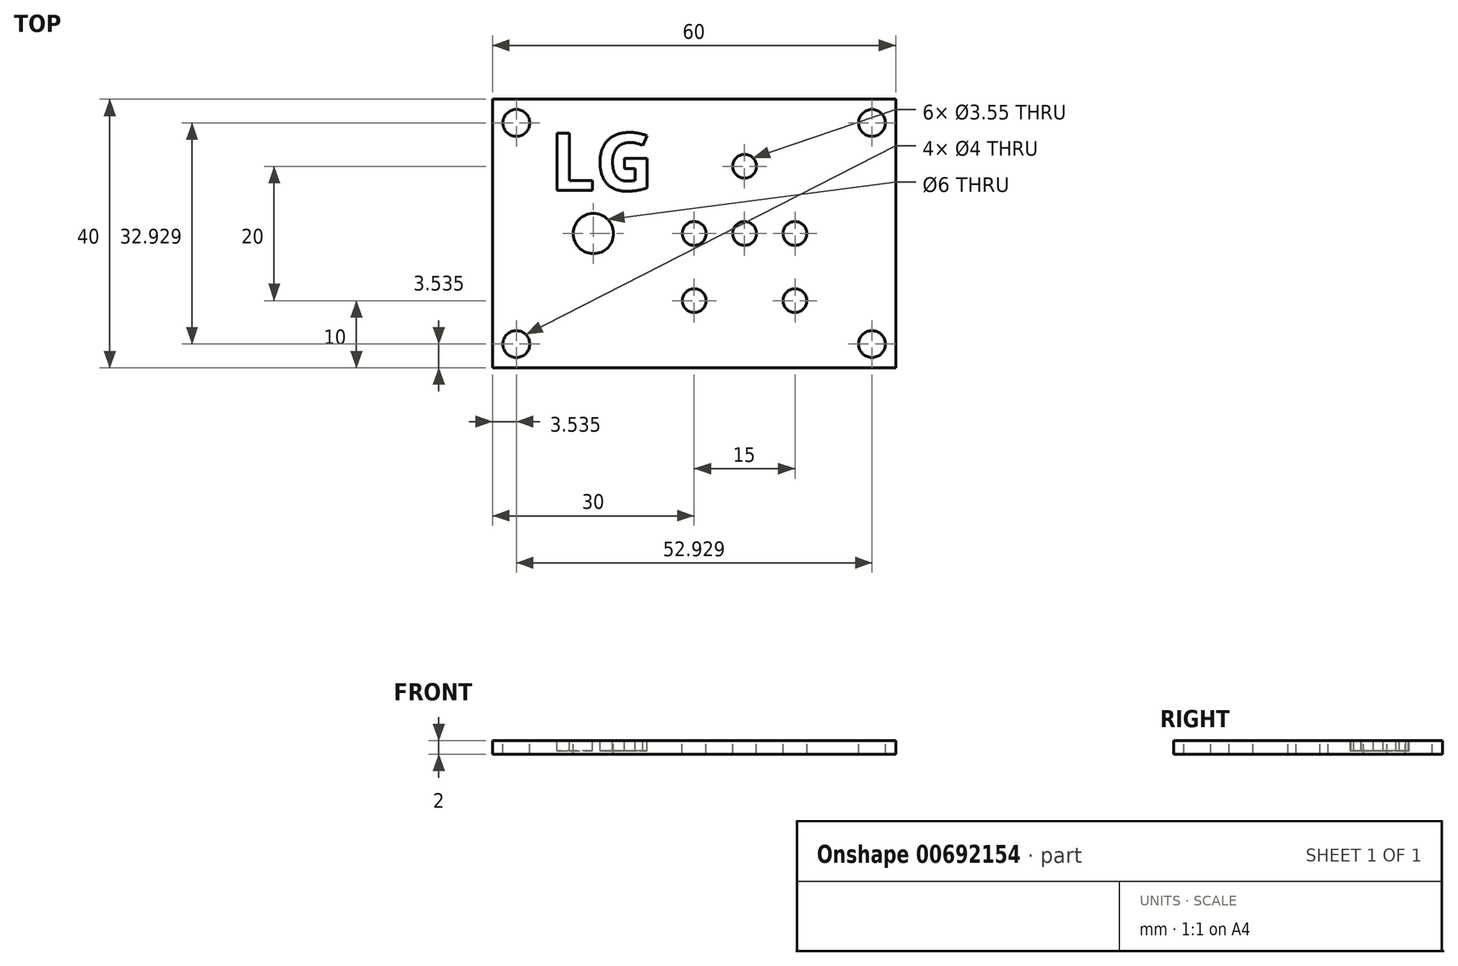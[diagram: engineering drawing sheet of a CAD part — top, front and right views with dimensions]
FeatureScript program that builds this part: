
annotation { "Feature Type Name" : "Feature", "Feature Type Description" : "" }
export const myFeature = defineFeature(function(context is Context, id is Id, definition is map)
    precondition{}
    {
        {
            var Q0;
            Q0=qCreatedBy(makeId("Top.planeOp"),FACE);
            var sketch = newSketch(context, id + "F0", { "sketchPlane" : qUnion([Q0])});
            skLineSegment(sketch, "E0.bottom", {"start": v(30, -20) * mm, "end": v(-30, -20) * mm});
            skLineSegment(sketch, "E0.top", {"start": v(30, 20) * mm, "end": v(-30, 20) * mm});
            skLineSegment(sketch, "E0.left", {"start": v(30, -20) * mm, "end": v(30, 20) * mm});
            skLineSegment(sketch, "E0.right", {"start": v(-30, -20) * mm, "end": v(-30, 20) * mm});
            skPoint(sketch, "E0.middle", {"position": v(0, 0) * mm});
            skLineSegment(sketch, "E1", {"start": v(-30, 0) * mm, "end": v(0, 0) * mm, "construction": true});
            skCircle(sketch, "E2", {"center": v(-15, 0) * mm, "radius": 3 * mm});
            skLineSegment(sketch, "E3", {"start": v(0, 0) * mm, "end": v(30, 0) * mm, "construction": true});
            skLineSegment(sketch, "E4", {"start": v(15, 0) * mm, "end": v(15, 20) * mm, "construction": true});
            skLineSegment(sketch, "E5", {"start": v(15, 0) * mm, "end": v(15, -20) * mm, "construction": true});
            skLineSegment(sketch, "E6", {"start": v(15, 10) * mm, "end": v(30, 10) * mm, "construction": true});
            skLineSegment(sketch, "E7", {"start": v(15, 10) * mm, "end": v(15, 4) * mm, "construction": true});
            skLineSegment(sketch, "E8", {"start": v(-30, 20) * mm, "end": v(-26.46, 16.46) * mm, "construction": true});
            skLineSegment(sketch, "E9", {"start": v(-30, -20) * mm, "end": v(-26.46, -16.46) * mm, "construction": true});
            skLineSegment(sketch, "E10", {"start": v(30, 20) * mm, "end": v(26.46, 16.46) * mm, "construction": true});
            skLineSegment(sketch, "E11", {"start": v(30, -20) * mm, "end": v(26.46, -16.46) * mm, "construction": true});
            skCircle(sketch, "E12", {"center": v(-26.46, 16.46) * mm, "radius": 2 * mm});
            skCircle(sketch, "E13", {"center": v(-26.46, -16.46) * mm, "radius": 2 * mm});
            skCircle(sketch, "E14", {"center": v(26.46, -16.46) * mm, "radius": 2 * mm});
            skCircle(sketch, "E15", {"center": v(26.46, 16.46) * mm, "radius": 2 * mm});
            skLineSegment(sketch, "E16", {"start": v(0, 0) * mm, "end": v(15, 0) * mm, "construction": true});
            skLineSegment(sketch, "E17", {"start": v(15, 0) * mm, "end": v(30, 0) * mm, "construction": true});
            skPoint(sketch, "E18.firstSnap0", {"position": v(-28.23, 18.23) * mm});
            skCircle(sketch, "E19", {"center": v(0, 0) * mm, "radius": 1.77 * mm});
            skCircle(sketch, "E20", {"center": v(15, 0) * mm, "radius": 1.77 * mm});
            skLineSegment(sketch, "E21", {"start": v(0, 20) * mm, "end": v(0, -20) * mm, "construction": true});
            skLineSegment(sketch, "E22", {"start": v(0, 20) * mm, "end": v(15, 20) * mm, "construction": true});
            skLineSegment(sketch, "E23", {"start": v(7.5, 20) * mm, "end": v(7.5, 0) * mm, "construction": true});
            skLineSegment(sketch, "E24", {"start": v(7.5, 0) * mm, "end": v(7.5, -20) * mm, "construction": true});
            skCircle(sketch, "E25", {"center": v(7.5, 10) * mm, "radius": 1.77 * mm});
            skCircle(sketch, "E26", {"center": v(7.5, 0) * mm, "radius": 1.77 * mm});
            skLineSegment(sketch, "E27", {"start": v(0, 0) * mm, "end": v(0, -20) * mm, "construction": true});
            skCircle(sketch, "E28", {"center": v(0, -10) * mm, "radius": 1.77 * mm});
            skCircle(sketch, "E29", {"center": v(15, -10) * mm, "radius": 1.77 * mm});
            skLineSegment(sketch, "E30.bottom", {"start": v(-26.46, 16.46) * mm, "end": v(26.46, 16.46) * mm, "construction": true});
            skLineSegment(sketch, "E30.top", {"start": v(-26.46, -16.46) * mm, "end": v(26.46, -16.46) * mm, "construction": true});
            skLineSegment(sketch, "E30.left", {"start": v(-26.46, 16.46) * mm, "end": v(-26.46, -16.46) * mm, "construction": true});
            skLineSegment(sketch, "E30.right", {"start": v(26.46, 16.46) * mm, "end": v(26.46, -16.46) * mm, "construction": true});
            skSolve(sketch);
        }
        {
            var Q0;
            Q0=makeQuery(id+"F0.imprint","IMPRINT",FACE,{"disambiguationData":[TD([[makeQuery(id+"F0.imprint","IMPRINT",EDGE,{"derivedFrom":sQuery(id+"F0.wireOp",EDGE,"E0.bottom")}),-1.0]])]});
            extrude(context, id + "F1", {"entities" : qUnion([Q0]), "oppositeDirection" : true, "depth" : 2 * mm, "offsetDistance" : 25 * mm});
        }
        {
            var Q0;
            Q0=makeQuery(id+"F1.opExtrude","CAP_FACE",FACE,{"disambiguationData":[OSD([sQuery(id+"F0.wireOp",EDGE,"E0.bottom"),sQuery(id+"F0.wireOp",EDGE,"E0.top"),sQuery(id+"F0.wireOp",EDGE,"E0.left"),sQuery(id+"F0.wireOp",EDGE,"E0.right"),sQuery(id+"F0.wireOp",EDGE,"E2"),sQuery(id+"F0.wireOp",EDGE,"7hUV5i3W-bibG-1Lyq-3cFw-TaZDMb2XdGYd"),sQuery(id+"F0.wireOp",EDGE,"6SDKNYt0-Fqy5-TUR7-WXC3-41Z6ryFEjSeN"),sQuery(id+"F0.wireOp",EDGE,"E12"),sQuery(id+"F0.wireOp",EDGE,"E13"),sQuery(id+"F0.wireOp",EDGE,"E14"),sQuery(id+"F0.wireOp",EDGE,"E15"),sQuery(id+"F0.wireOp",EDGE,"FHc03Ag4-hQKU-7Hip-CNxW-fxphlJstFxZc"),sQuery(id+"F0.wireOp",EDGE,"rXKjmy1a-UXCm-gvVB-WE5C-CkgM09U8epoa"),sQuery(id+"F0.wireOp",EDGE,"1mli0hnT-Aaig-HHSW-9qeN-4sPPPm6kkbj5"),sQuery(id+"F0.wireOp",EDGE,"S84RuD43-9y0r-6jC6-vyR3-SVG9hiXAwePf")])],"isStart":true});
            var sketch = newSketch(context, id + "F2", { "sketchPlane" : qUnion([Q0])});
            skText(sketch, "E31", { "text": "LG", "fontName": "OpenSans-Bold.ttf"});
            const initialGuessF2  = {"E31": [-0.02145, 0.00641, 1, 0, 0.0086]};
            skSetInitialGuess(sketch, initialGuessF2);
            skSolve(sketch);
        }
        {
            var Q0;
            Q0 = qSketchRegion(id + "F2", true);
            extrude(context, id + "F3", {"entities" : qUnion([Q0]), "operationType" : NewBodyOperationType.REMOVE, "oppositeDirection" : true, "depth" : 1.5 * mm, "offsetDistance" : 25 * mm});
        }
    });
